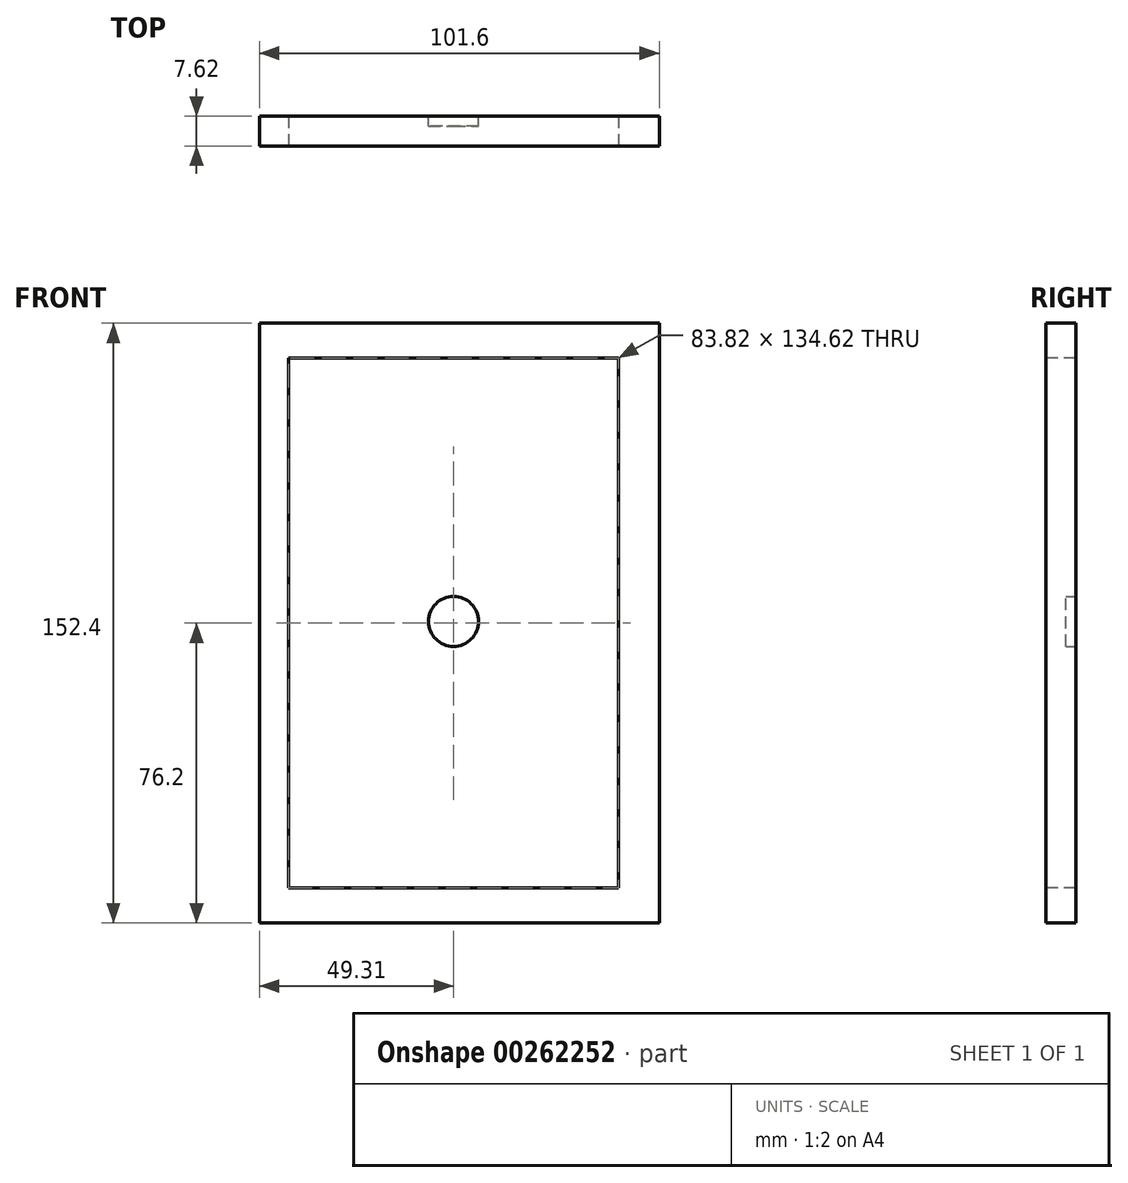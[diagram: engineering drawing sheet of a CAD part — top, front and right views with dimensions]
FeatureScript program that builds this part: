
annotation { "Feature Type Name" : "Feature", "Feature Type Description" : "" }
export const myFeature = defineFeature(function(context is Context, id is Id, definition is map)
    precondition{}
    {
        {
            var Q0;
            Q0=qCreatedBy(makeId("Front.planeOp"),FACE);
            var sketch = newSketch(context, id + "F0", { "sketchPlane" : qUnion([Q0])});
            skLineSegment(sketch, "E0.bottom", {"start": v(52.29, -76.2) * mm, "end": v(-49.31, -76.2) * mm});
            skLineSegment(sketch, "E0.top", {"start": v(52.29, 76.2) * mm, "end": v(-49.31, 76.2) * mm});
            skLineSegment(sketch, "E0.left", {"start": v(52.29, -76.2) * mm, "end": v(52.29, 76.2) * mm});
            skLineSegment(sketch, "E0.right", {"start": v(-49.31, -76.2) * mm, "end": v(-49.31, 76.2) * mm});
            skPoint(sketch, "E0.middle", {"position": v(1.49, 0) * mm});
            skSolve(sketch);
        }
        {
            var Q0;
            Q0=makeQuery(id+"F0.imprint","IMPRINT",FACE,{"disambiguationData":[TD([[makeQuery(id+"F0.imprint","IMPRINT",EDGE,{"derivedFrom":sQuery(id+"F0.wireOp",EDGE,"E0.bottom")}),-1.0]])]});
            extrude(context, id + "F1", {"entities" : qUnion([Q0]), "depth" : 7.62 * mm});
        }
        {
            var Q0;
            Q0=makeQuery(id+"F1.opExtrude","CAP_FACE",FACE,{"disambiguationData":[OSD([sQuery(id+"F0.wireOp",EDGE,"E0.bottom"),sQuery(id+"F0.wireOp",EDGE,"E0.top"),sQuery(id+"F0.wireOp",EDGE,"E0.left"),sQuery(id+"F0.wireOp",EDGE,"E0.right")])],"isStart":false});
            var sketch = newSketch(context, id + "F2", { "sketchPlane" : qUnion([Q0])});
            skLineSegment(sketch, "E1.bottom", {"start": v(41.91, -67.31) * mm, "end": v(-41.91, -67.31) * mm});
            skLineSegment(sketch, "E1.top", {"start": v(41.91, 67.31) * mm, "end": v(-41.91, 67.31) * mm});
            skLineSegment(sketch, "E1.left", {"start": v(41.91, -67.31) * mm, "end": v(41.91, 67.31) * mm});
            skLineSegment(sketch, "E1.right", {"start": v(-41.91, -67.31) * mm, "end": v(-41.91, 67.31) * mm});
            skPoint(sketch, "E1.middle", {"position": v(0, 0) * mm});
            skSolve(sketch);
        }
        {
            var Q0;
            Q0=makeQuery(id+"F2.imprint","IMPRINT",FACE,{"disambiguationData":[TD([[makeQuery(id+"F2.imprint","IMPRINT",EDGE,{"derivedFrom":sQuery(id+"F2.wireOp",EDGE,"E1.bottom")}),-1.0]])]});
            extrude(context, id + "F3", {"entities" : qUnion([Q0]), "operationType" : NewBodyOperationType.REMOVE, "oppositeDirection" : true, "depth" : 25.4 * mm});
        }
        {
            var Q0;
            Q0=qCreatedBy(makeId("Front.planeOp"),FACE);
            var sketch = newSketch(context, id + "F4", { "sketchPlane" : qUnion([Q0])});
            skCircle(sketch, "E2", {"center": v(0, 0.44) * mm, "radius": 6.35 * mm});
            skSolve(sketch);
        }
        {
            var Q0;
            Q0=makeQuery(id+"F4.imprint","IMPRINT",FACE,{"disambiguationData":[TD([[makeQuery(id+"F4.imprint","IMPRINT",EDGE,{"derivedFrom":sQuery(id+"F4.wireOp",EDGE,"E2")}),1.0]])]});
            extrude(context, id + "F5", {"entities" : qUnion([Q0]), "depth" : 2.54 * mm});
        }
    });
